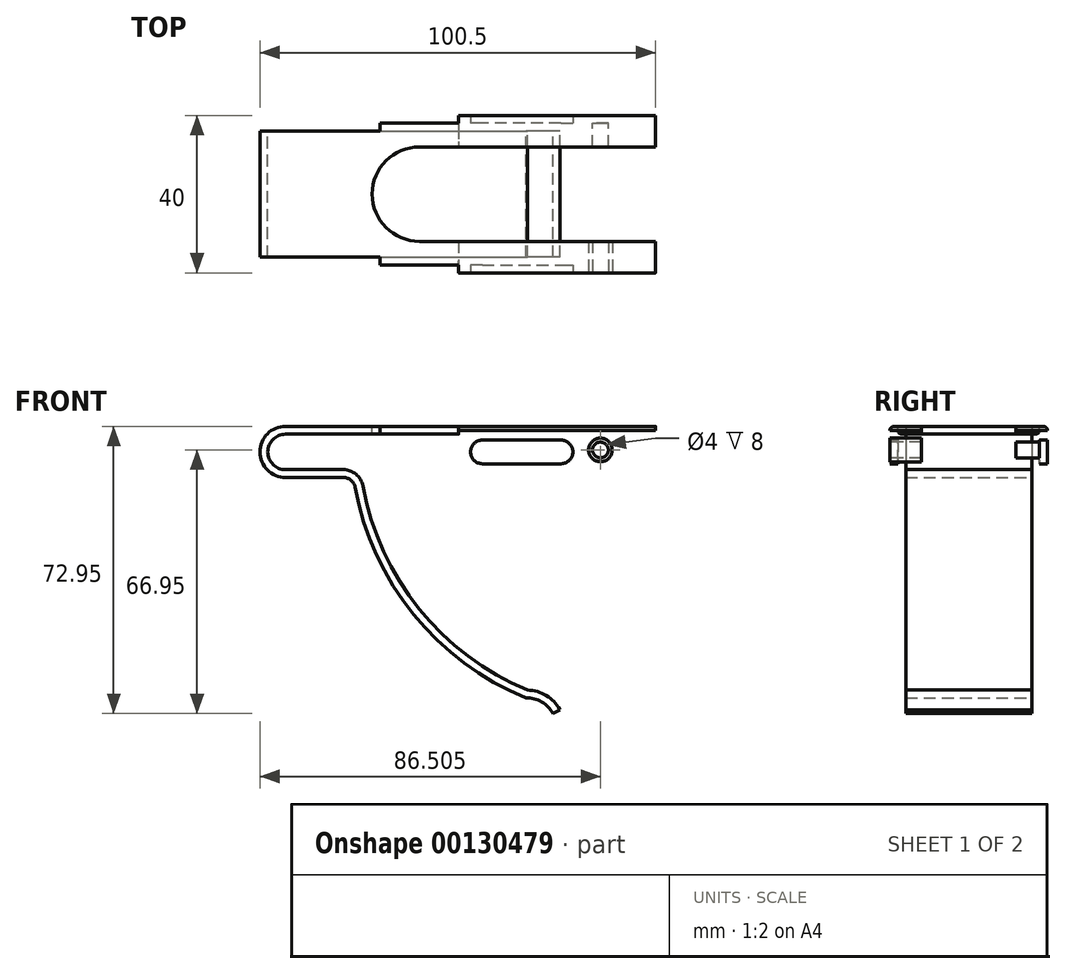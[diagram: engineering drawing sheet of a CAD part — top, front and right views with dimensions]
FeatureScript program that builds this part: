
annotation { "Feature Type Name" : "Feature", "Feature Type Description" : "" }
export const myFeature = defineFeature(function(context is Context, id is Id, definition is map)
    precondition{}
    {
        {
            var Q0;
            Q0=qCreatedBy(makeId("Front.planeOp"),FACE);
            var sketch = newSketch(context, id + "F0", { "sketchPlane" : qUnion([Q0])});
            skArc(sketch, "E0", {"start": v(-78.26, 4.5) * mm, "mid": v(-82.76, 0) * mm, "end": v(-78.26, -4.5) * mm});
            skLineSegment(sketch, "E1", {"start": v(-78.26, 4.5) * mm, "end": v(15.74, 4.5) * mm});
            skLineSegment(sketch, "E2", {"start": v(-78.26, -4.5) * mm, "end": v(-63.54, -4.5) * mm});
            skArc(sketch, "E3", {"start": v(-58.63, -8.6) * mm, "mid": v(-44.3, -39.84) * mm, "end": v(-16.81, -60.5) * mm});
            skArc(sketch, "E4", {"start": v(-8.59, -65.5) * mm, "mid": v(-12.02, -61.89) * mm, "end": v(-16.81, -60.5) * mm});
            skPoint(sketch, "E5.visualSharp", {"position": v(-59.26, -4.5) * mm});
            skArc(sketch, "E5.filletArc", {"start": v(-58.63, -8.6) * mm, "mid": v(-60.34, -5.66) * mm, "end": v(-63.54, -4.5) * mm});
            skLineSegment(sketch, "E6.0", {"start": v(-78.26, 6.5) * mm, "end": v(15.74, 6.5) * mm});
            skArc(sketch, "E6.1", {"start": v(-78.26, 6.5) * mm, "mid": v(-84.76, 0) * mm, "end": v(-78.26, -6.5) * mm});
            skArc(sketch, "E6.2", {"start": v(-10.34, -66.45) * mm, "mid": v(-13.22, -63.5) * mm, "end": v(-17.2, -62.5) * mm});
            skArc(sketch, "E6.3", {"start": v(-60.6, -8.96) * mm, "mid": v(-45.72, -41.26) * mm, "end": v(-17.2, -62.5) * mm});
            skArc(sketch, "E6.4", {"start": v(-60.6, -8.96) * mm, "mid": v(-61.62, -7.2) * mm, "end": v(-63.54, -6.5) * mm});
            skLineSegment(sketch, "E6.5", {"start": v(-78.26, -6.5) * mm, "end": v(-63.54, -6.5) * mm});
            skLineSegment(sketch, "E7", {"start": v(15.74, 6.5) * mm, "end": v(15.74, 4.5) * mm});
            skLineSegment(sketch, "E8", {"start": v(-8.59, -65.5) * mm, "end": v(-10.34, -66.45) * mm});
            skSolve(sketch);
        }
        {
            var Q0;
            Q0=makeQuery(id+"F0.imprint","IMPRINT",FACE,{"disambiguationData":[TD([[makeQuery(id+"F0.imprint","IMPRINT",EDGE,{"derivedFrom":sQuery(id+"F0.wireOp",EDGE,"E0")}),-1.0]])]});
            extrude(context, id + "F1", {"entities" : qUnion([Q0]), "depth" : 16 * mm});
        }
        {
            var Q0;
            Q0=makeQuery(id+"F1.opExtrude","SWEPT_FACE",FACE,{"disambiguationData":[OSD([sQuery(id+"F0.wireOp",EDGE,"E6.0")])]});
            var sketch = newSketch(context, id + "F2", { "sketchPlane" : qUnion([Q0])});
            skLineSegment(sketch, "E9.bottom", {"start": v(15.74, -16) * mm, "end": v(-54.26, -16) * mm});
            skLineSegment(sketch, "E9.top", {"start": v(15.74, -18) * mm, "end": v(-54.26, -18) * mm});
            skLineSegment(sketch, "E9.left", {"start": v(15.74, -16) * mm, "end": v(15.74, -18) * mm});
            skLineSegment(sketch, "E9.right", {"start": v(-54.26, -16) * mm, "end": v(-54.26, -18) * mm});
            skSolve(sketch);
        }
        {
            var Q0;
            Q0=makeQuery(id+"F2.imprint","IMPRINT",FACE,{"disambiguationData":[TD([[makeQuery(id+"F2.imprint","IMPRINT",EDGE,{"derivedFrom":sQuery(id+"F2.wireOp",EDGE,"E9.bottom")}),-1.0]])]});
            extrude(context, id + "F3", {"entities" : qUnion([Q0]), "operationType" : NewBodyOperationType.ADD, "oppositeDirection" : true, "depth" : 2 * mm});
        }
        {
            var Q0;
            Q0=makeQuery(id+"F3.opExtrude","SWEPT_FACE",FACE,{"disambiguationData":[OSD([sQuery(id+"F2.wireOp",EDGE,"E9.top")])]});
            var sketch = newSketch(context, id + "F4", { "sketchPlane" : qUnion([Q0])});
            skLineSegment(sketch, "E10.bottom", {"start": v(15.74, 6.5) * mm, "end": v(-34.26, 6.5) * mm});
            skLineSegment(sketch, "E10.top", {"start": v(15.74, -5.5) * mm, "end": v(-34.26, -5.5) * mm});
            skLineSegment(sketch, "E10.left", {"start": v(15.74, 6.5) * mm, "end": v(15.74, -5.5) * mm});
            skLineSegment(sketch, "E10.right", {"start": v(-34.26, 6.5) * mm, "end": v(-34.26, -5.5) * mm});
            skSolve(sketch);
        }
        {
            var Q0;
            {var subQ0=sQuery(id+"F4.wireOp",EDGE,"E10.top");Q0=makeQuery(id+"F4.imprint","IMPRINT",FACE,{"disambiguationData":[TD([[makeQuery(id+"F4.imprint","IMPRINT",EDGE,{"derivedFrom":subQ0}),-1.0]])]});}
            var Q1;
            {var subQ0=sQuery(id+"F4.wireOp",EDGE,"E10.bottom");Q1=makeQuery(id+"F4.imprint","IMPRINT",FACE,{"disambiguationData":[TD([[makeQuery(id+"F4.imprint","IMPRINT",EDGE,{"derivedFrom":subQ0}),1.0]])]});}
            extrude(context, id + "F5", {"entities" : qUnion([Q0, Q1]), "operationType" : NewBodyOperationType.ADD, "depth" : 2 * mm});
        }
        {
            var Q0;
            Q0=makeQuery(id+"F5.opExtrude","CAP_EDGE",EDGE,{"disambiguationData":[OSD([sQuery(id+"F4.wireOp",EDGE,"E10.bottom")])],"isStart":false});
            var Q1;
            {var subQ0=sQuery(id+"F2.wireOp",EDGE,"E9.top");Q1=makeQuery(id+"F5.boolean.opBoolean","SPLIT",EDGE,{"disambiguationData":[TD([makeQuery(id+"F1.opExtrude","SWEPT_FACE",FACE,{"disambiguationData":[OSD([sQuery(id+"F0.wireOp",EDGE,"E7")])]})])],"derivedFrom":makeQuery(id+"F3.opExtrude","CAP_EDGE",EDGE,{"disambiguationData":[OSD([subQ0])],"isStart":false})});}
            fillet(context, id + "F6", {"entities" : qUnion([Q0, Q1]), "radius" : 1 * mm, "tangentPropagation" : true, "allowEdgeOverflow" : false});
        }
        {
            var Q0;
            Q0=makeQuery(id+"F1.opExtrude","SWEPT_BODY",BODY,{"disambiguationData":[OSD([sQuery(id+"F0.wireOp",EDGE,"E0"),sQuery(id+"F0.wireOp",EDGE,"E1"),sQuery(id+"F0.wireOp",EDGE,"E2"),sQuery(id+"F0.wireOp",EDGE,"E3"),sQuery(id+"F0.wireOp",EDGE,"E4"),sQuery(id+"F0.wireOp",EDGE,"E5.filletArc"),sQuery(id+"F0.wireOp",EDGE,"E6.0"),sQuery(id+"F0.wireOp",EDGE,"E6.1"),sQuery(id+"F0.wireOp",EDGE,"E6.2"),sQuery(id+"F0.wireOp",EDGE,"E6.3"),sQuery(id+"F0.wireOp",EDGE,"E6.4"),sQuery(id+"F0.wireOp",EDGE,"E6.5"),sQuery(id+"F0.wireOp",EDGE,"E7"),sQuery(id+"F0.wireOp",EDGE,"E8")])]});
            var Q1;
            Q1=makeQuery(id+"F1.opExtrude","CAP_FACE",FACE,{"disambiguationData":[OSD([sQuery(id+"F0.wireOp",EDGE,"E0"),sQuery(id+"F0.wireOp",EDGE,"E1"),sQuery(id+"F0.wireOp",EDGE,"E2"),sQuery(id+"F0.wireOp",EDGE,"E3"),sQuery(id+"F0.wireOp",EDGE,"E4"),sQuery(id+"F0.wireOp",EDGE,"E5.filletArc"),sQuery(id+"F0.wireOp",EDGE,"E6.0"),sQuery(id+"F0.wireOp",EDGE,"E6.1"),sQuery(id+"F0.wireOp",EDGE,"E6.2"),sQuery(id+"F0.wireOp",EDGE,"E6.3"),sQuery(id+"F0.wireOp",EDGE,"E6.4"),sQuery(id+"F0.wireOp",EDGE,"E6.5"),sQuery(id+"F0.wireOp",EDGE,"E7"),sQuery(id+"F0.wireOp",EDGE,"E8")])],"isStart":true});
            mirror(context, id + "F7", {"operationType" : NewBodyOperationType.ADD, "entities" : qUnion([Q0]), "mirrorPlane" : qUnion([Q1])});
        }
        {
            var Q0;
            {var subQ0=makeQuery(id+"F5.boolean.opBoolean","MERGE",FACE,{"derivedFrom":[makeQuery(id+"F3.boolean.opBoolean","MERGE",FACE,{"derivedFrom":[makeQuery(id+"F1.opExtrude","SWEPT_FACE",FACE,{"disambiguationData":[OSD([sQuery(id+"F0.wireOp",EDGE,"E6.0")])]}),makeQuery(id+"F3.opExtrude","CAP_FACE",FACE,{"disambiguationData":[OSD([sQuery(id+"F2.wireOp",EDGE,"E9.bottom"),sQuery(id+"F2.wireOp",EDGE,"E9.top"),sQuery(id+"F2.wireOp",EDGE,"E9.left"),sQuery(id+"F2.wireOp",EDGE,"E9.right")])],"isStart":true})]}),makeQuery(id+"F5.opExtrude","SWEPT_FACE",FACE,{"disambiguationData":[OSD([sQuery(id+"F4.wireOp",EDGE,"E10.bottom")])]})]});Q0=makeQuery(id+"F7.boolean.opBoolean","MERGE",FACE,{"derivedFrom":[subQ0,makeQuery(id+"F7.opPattern","COPY",FACE,{"derivedFrom":subQ0,"instanceName":"1"})]});}
            var sketch = newSketch(context, id + "F8", { "sketchPlane" : qUnion([Q0])});
            skArc(sketch, "E11", {"start": v(-44.26, 12) * mm, "mid": v(-56.26, 0) * mm, "end": v(-44.26, -12) * mm});
            skLineSegment(sketch, "E12", {"start": v(-44.26, 12) * mm, "end": v(15.74, 12) * mm});
            skLineSegment(sketch, "E13", {"start": v(-44.26, -12) * mm, "end": v(15.74, -12) * mm});
            skSolve(sketch);
        }
        {
            var Q0;
            Q0=makeQuery(id+"F8.imprint","IMPRINT",FACE,{"disambiguationData":[TD([[makeQuery(id+"F8.imprint","IMPRINT",EDGE,{"derivedFrom":sQuery(id+"F8.wireOp",EDGE,"E11")}),1.0]])]});
            extrude(context, id + "F9", {"entities" : qUnion([Q0]), "operationType" : NewBodyOperationType.REMOVE, "oppositeDirection" : true, "depth" : 2 * mm});
        }
        {
            var Q0;
            Q0=makeQuery(id+"F5.opExtrude","CAP_FACE",FACE,{"disambiguationData":[OSD([sQuery(id+"F4.wireOp",EDGE,"E10.bottom"),sQuery(id+"F4.wireOp",EDGE,"E10.top"),sQuery(id+"F4.wireOp",EDGE,"E10.left"),sQuery(id+"F4.wireOp",EDGE,"E10.right")])],"isStart":false});
            var sketch = newSketch(context, id + "F10", { "sketchPlane" : qUnion([Q0])});
            skLineSegment(sketch, "E14", {"start": v(-28.26, 0) * mm, "end": v(-8.26, 0) * mm});
            skPoint(sketch, "E14.startSnap0", {"position": v(-34.26, 0) * mm});
            skPoint(sketch, "E14.endSnap0", {"position": v(-34.26, 0) * mm});
            skArc(sketch, "E15.0.startCap", {"start": v(-28.26, -3) * mm, "mid": v(-31.26, 0) * mm, "end": v(-28.26, 3) * mm});
            skArc(sketch, "E15.0.endCap", {"start": v(-8.26, 3) * mm, "mid": v(-5.26, 0) * mm, "end": v(-8.26, -3) * mm});
            skLineSegment(sketch, "E15.0.left", {"start": v(-28.26, 3) * mm, "end": v(-8.26, 3) * mm});
            skLineSegment(sketch, "E15.0.right", {"start": v(-28.26, -3) * mm, "end": v(-8.26, -3) * mm});
            skSolve(sketch);
        }
        {
            var Q0;
            Q0=makeQuery(id+"F10.imprint","IMPRINT",FACE,{"disambiguationData":[TD([[makeQuery(id+"F10.imprint","IMPRINT",EDGE,{"derivedFrom":sQuery(id+"F10.wireOp",EDGE,"E15.0.startCap")}),-1.0]])]});
            extrude(context, id + "F11", {"entities" : qUnion([Q0]), "operationType" : NewBodyOperationType.REMOVE, "endBound" : BoundingType.THROUGH_ALL, "oppositeDirection" : true, "depth" : 25 * mm});
        }
        {
            var Q0;
            Q0=makeQuery(id+"F5.opExtrude","CAP_FACE",FACE,{"disambiguationData":[OSD([sQuery(id+"F4.wireOp",EDGE,"E10.bottom"),sQuery(id+"F4.wireOp",EDGE,"E10.top"),sQuery(id+"F4.wireOp",EDGE,"E10.left"),sQuery(id+"F4.wireOp",EDGE,"E10.right")])],"isStart":false});
            var sketch = newSketch(context, id + "F12", { "sketchPlane" : qUnion([Q0])});
            skPoint(sketch, "E16", {"position": v(1.74, 0.5) * mm});
            skCircle(sketch, "E17", {"center": v(1.74, 0.5) * mm, "radius": 2 * mm});
            skCircle(sketch, "E18.0", {"center": v(1.74, 0.5) * mm, "radius": 3 * mm});
            skSolve(sketch);
        }
        {
            var Q0;
            Q0=makeQuery(id+"F12.imprint","IMPRINT",FACE,{"disambiguationData":[TD([[makeQuery(id+"F12.imprint","IMPRINT",EDGE,{"derivedFrom":sQuery(id+"F12.wireOp",EDGE,"E17")}),1.0]])]});
            extrude(context, id + "F13", {"entities" : qUnion([Q0]), "operationType" : NewBodyOperationType.REMOVE, "endBound" : BoundingType.THROUGH_ALL, "oppositeDirection" : true, "depth" : 25 * mm});
        }
        {
            var Q0;
            Q0=makeQuery(id+"F12.imprint","IMPRINT",FACE,{"disambiguationData":[TD([[makeQuery(id+"F12.imprint","IMPRINT",EDGE,{"derivedFrom":sQuery(id+"F12.wireOp",EDGE,"E17")}),-1.0]])]});
            extrude(context, id + "F14", {"entities" : qUnion([Q0]), "operationType" : NewBodyOperationType.ADD, "oppositeDirection" : true, "depth" : 8 * mm});
        }
        {
            var Q0;
            Q0=makeQuery(id+"F7.opPattern","COPY",FACE,{"derivedFrom":makeQuery(id+"F5.opExtrude","CAP_FACE",FACE,{"disambiguationData":[OSD([sQuery(id+"F4.wireOp",EDGE,"E10.bottom"),sQuery(id+"F4.wireOp",EDGE,"E10.top"),sQuery(id+"F4.wireOp",EDGE,"E10.left"),sQuery(id+"F4.wireOp",EDGE,"E10.right")])],"isStart":true}),"instanceName":"1"});
            var sketch = newSketch(context, id + "F15", { "sketchPlane" : qUnion([Q0])});
            skCircle(sketch, "E19.0", {"center": v(1.74, 0.5) * mm, "radius": 2 * mm});
            skCircle(sketch, "E20.0", {"center": v(1.74, 0.5) * mm, "radius": 3 * mm});
            skSolve(sketch);
        }
        {
            var Q0;
            Q0=makeQuery(id+"F15.imprint","IMPRINT",FACE,{"disambiguationData":[TD([[makeQuery(id+"F15.imprint","IMPRINT",EDGE,{"derivedFrom":sQuery(id+"F15.wireOp",EDGE,"E19.0")}),1.0]])]});
            extrude(context, id + "F16", {"entities" : qUnion([Q0]), "operationType" : NewBodyOperationType.ADD, "depth" : 6 * mm});
        }
    });
